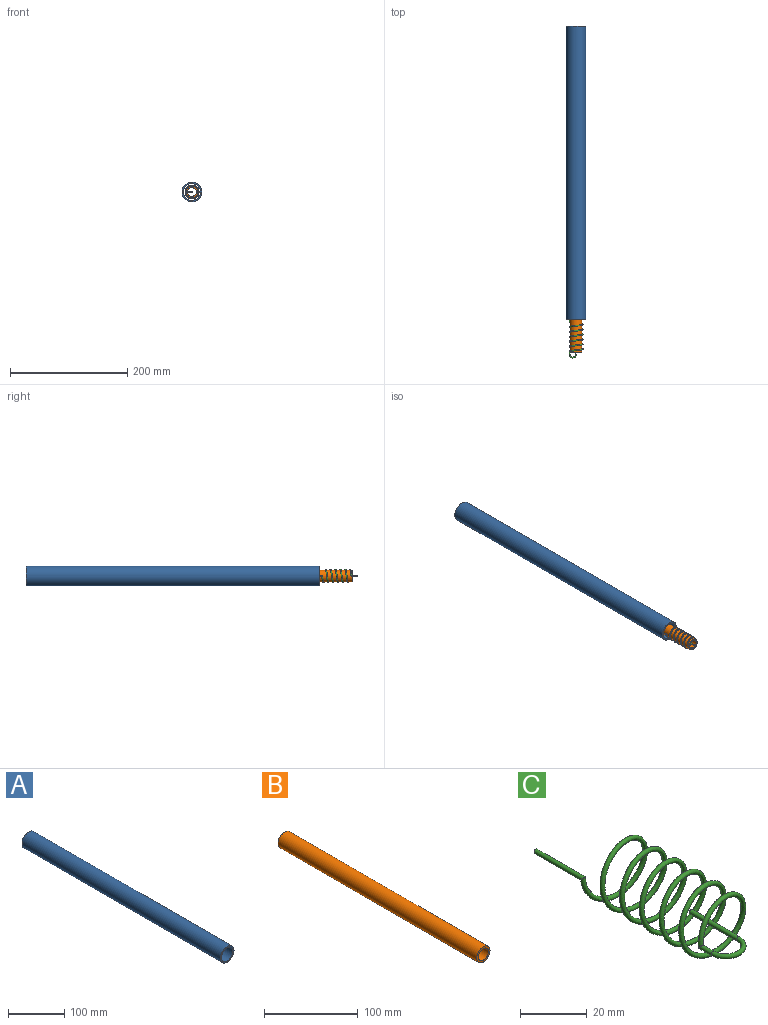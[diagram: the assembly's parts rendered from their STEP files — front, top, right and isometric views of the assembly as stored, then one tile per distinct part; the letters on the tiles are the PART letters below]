
ASSEMBLY  parts=3 mates=2
PART A: 4 faces, bbox 34x500x34 mm
  f0: cylinder r=14.35mm len=500mm, axis (0,1,0), area 45081.9mm2, adj f2,f3
  f1: cylinder r=17mm len=500mm, axis (0,1,0), area 53407.1mm2, adj f2,f3
  f2: plane 34x34mm, normal (0,-1,0), area 261mm2, adj f0,f1
  f3: plane 34x34mm, normal (0,1,0), area 261mm2, adj f0,f1
PART B: 4 faces, bbox 20x300x20 mm
  f0: cylinder r=7.5mm len=300mm, axis (0,1,0), area 14137.2mm2, adj f2,f3
  f1: cylinder r=10mm len=300mm, axis (0,1,0), area 18849.6mm2, adj f2,f3
  f2: plane 20x20mm, normal (0,-1,0), area 137.4mm2, adj f0,f1
  f3: plane 20x20mm, normal (0,1,0), area 137.4mm2, adj f0,f1
PART C: 7 faces, bbox 23.9x81.6x23.4 mm
  f0: plane 1.5x1.5mm, normal (0,1,0), area 1.8mm2, adj f4
  f1: plane 1.5x1.5mm, normal (0,1,0), area 1.8mm2, adj f6
  f2: cylinder r=0.75mm len=5.67mm, axis (0,-1,0), area 22.6mm2, adj f3,f5
  f3: torus R=5.38mm, axis (0,0,1), area 79.6mm2, adj f2,f4
  f4: cylinder r=0.75mm len=20mm, axis (0,1,0), area 94.2mm2, adj f0,f3
  f5: bspline ~51.64x23.41mm, area 1966.2mm2, adj f2,f6
  f6: cylinder r=0.75mm len=20.67mm, axis (0,-1,0), area 94.2mm2, adj f1,f5
PLACE A t=(68.08,310.7,-70.96)mm
PLACE B t=(17,53.66,-29.28)mm
PLACE C t=(68.33,-193.79,-70.96)mm
MATE cylindrical A.f0 <-> B.f0  axis (0,1,0) through (68.08,60.7,-70.96)mm
MATE cylindrical C.f4 <-> B.f0  axis (0,1,0) through (68.08,-238.79,-70.96)mm
